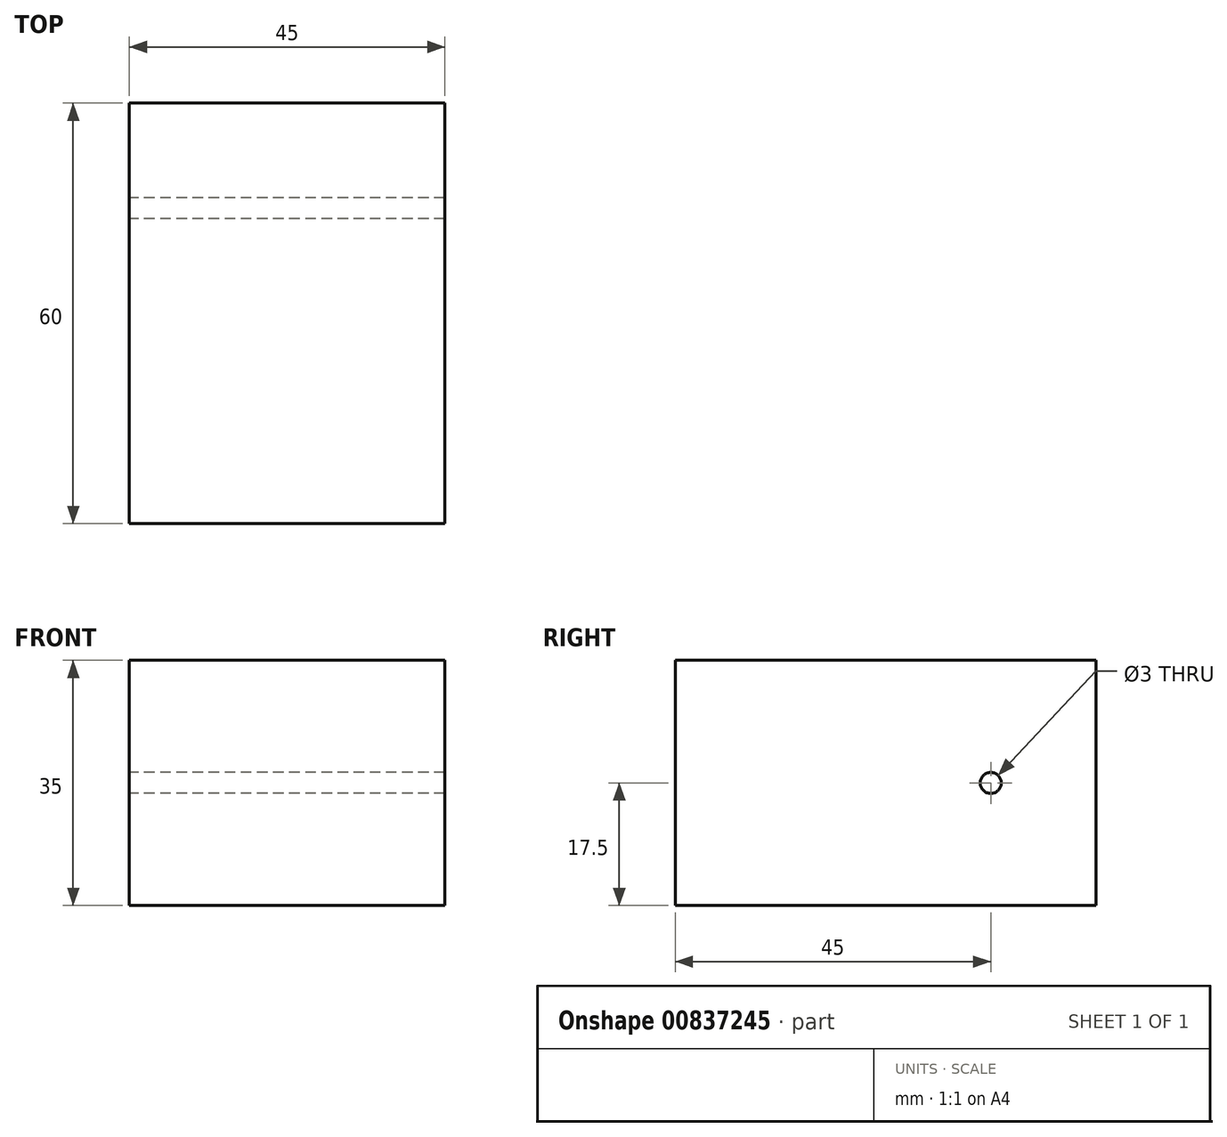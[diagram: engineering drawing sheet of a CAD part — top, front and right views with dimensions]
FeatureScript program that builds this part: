
annotation { "Feature Type Name" : "Feature", "Feature Type Description" : "" }
export const myFeature = defineFeature(function(context is Context, id is Id, definition is map)
    precondition{}
    {
        {
            var Q0;
            Q0=qCreatedBy(makeId("Right.planeOp"),FACE);
            var sketch = newSketch(context, id + "F0", { "sketchPlane" : qUnion([Q0])});
            skLineSegment(sketch, "E0.bottom", {"start": v(30, 17.5) * mm, "end": v(-30, 17.5) * mm});
            skLineSegment(sketch, "E0.top", {"start": v(30, -17.5) * mm, "end": v(-30, -17.5) * mm});
            skLineSegment(sketch, "E0.left", {"start": v(30, 17.5) * mm, "end": v(30, -17.5) * mm});
            skLineSegment(sketch, "E0.right", {"start": v(-30, 17.5) * mm, "end": v(-30, -17.5) * mm});
            skPoint(sketch, "E0.middle", {"position": v(0, 0) * mm});
            skCircle(sketch, "E1", {"center": v(15, 0) * mm, "radius": 1.5 * mm});
            skSolve(sketch);
        }
        {
            var Q0;
            Q0 = qSketchRegion(id + "F0", true);
            extrude(context, id + "F1", {"entities" : qUnion([Q0]), "depth" : 45 * mm, "offsetDistance" : 25.4 * mm});
        }
    });
